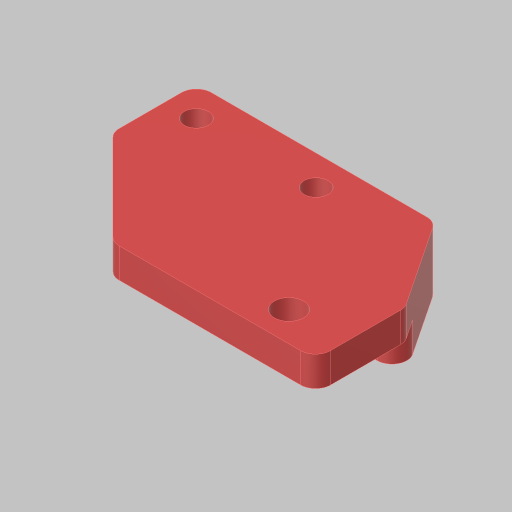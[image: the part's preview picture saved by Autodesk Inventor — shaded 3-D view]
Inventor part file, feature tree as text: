
AUTODESK INVENTOR PART (.ipt)
format: ipt  version: 2023.5 (Build 275446000, 446)  size: 178,688 bytes
history: native  units: in
note: dims shown in document units (in); Inventor stores cm internally (conversion verified against a paired STEP export)
features: sketch x6, extrude x3, fillet x3, hole x2, projected_geometry x2
ambient origin geometry x8: Origin, YZ Plane, XZ Plane, XY Plane, X Axis, Y Axis, Z Axis, Center Point
bodies: Solid1 (feature_tree)
feature tree (16):
  extrude  "Extrusion1"  Depth=1.5in
  hole  "Hole1"  [1 undecoded]
  hole  "Hole2"  [1 undecoded]
  fillet  "Fillet1"  Radius=0.125in
  extrude  "Extrusion2"  Depth=0.125in
  fillet  "Fillet2"  Radius=0.5in
  sketch  "Sketch5"  dims[d14=0.244in d15=0.75in d16=0.375in d17=0.25in d18=0.5635in d19=1.0in d20=0.8108in d21=0.125in]
  extrude  "Extrusion3"  Depth=0.25in TaperAngle=0.0deg
  fillet  "Fillet3"  Radius=0.125in
  sketch  "Sketch1"  dims[d0=2.5in d1=1.5in]
  sketch  "Sketch2"  dims[d2=0.25in d3=0.0in d4=1.005in]
  sketch  "Sketch3"  dims[d5=0.25in]
  sketch  "Sketch4"  dims[d6=0.201in d7=0.75in d8=0.385in d9=0.25in d10=0.5635in d11=1.0in d12=0.8108in d13=0.25in]
  sketch  "Sketch6"  dims[d22=0.25in d23=0.75in d24=0.5in d25=0.25in d26=0.0in d27=0.125in d28=0.777in d29=0.8in d30=0.8in d31=0.25in d32=0.0in d33=0.125in]
  projected_geometry  "Projected Loop1"
  projected_geometry  "Project Cut Edges1"
note: 2 required parameter values undecoded (feature->parameter linkage not recoverable at this tier; creation-order binding heuristic only, values carry confidence <= 0.55)
